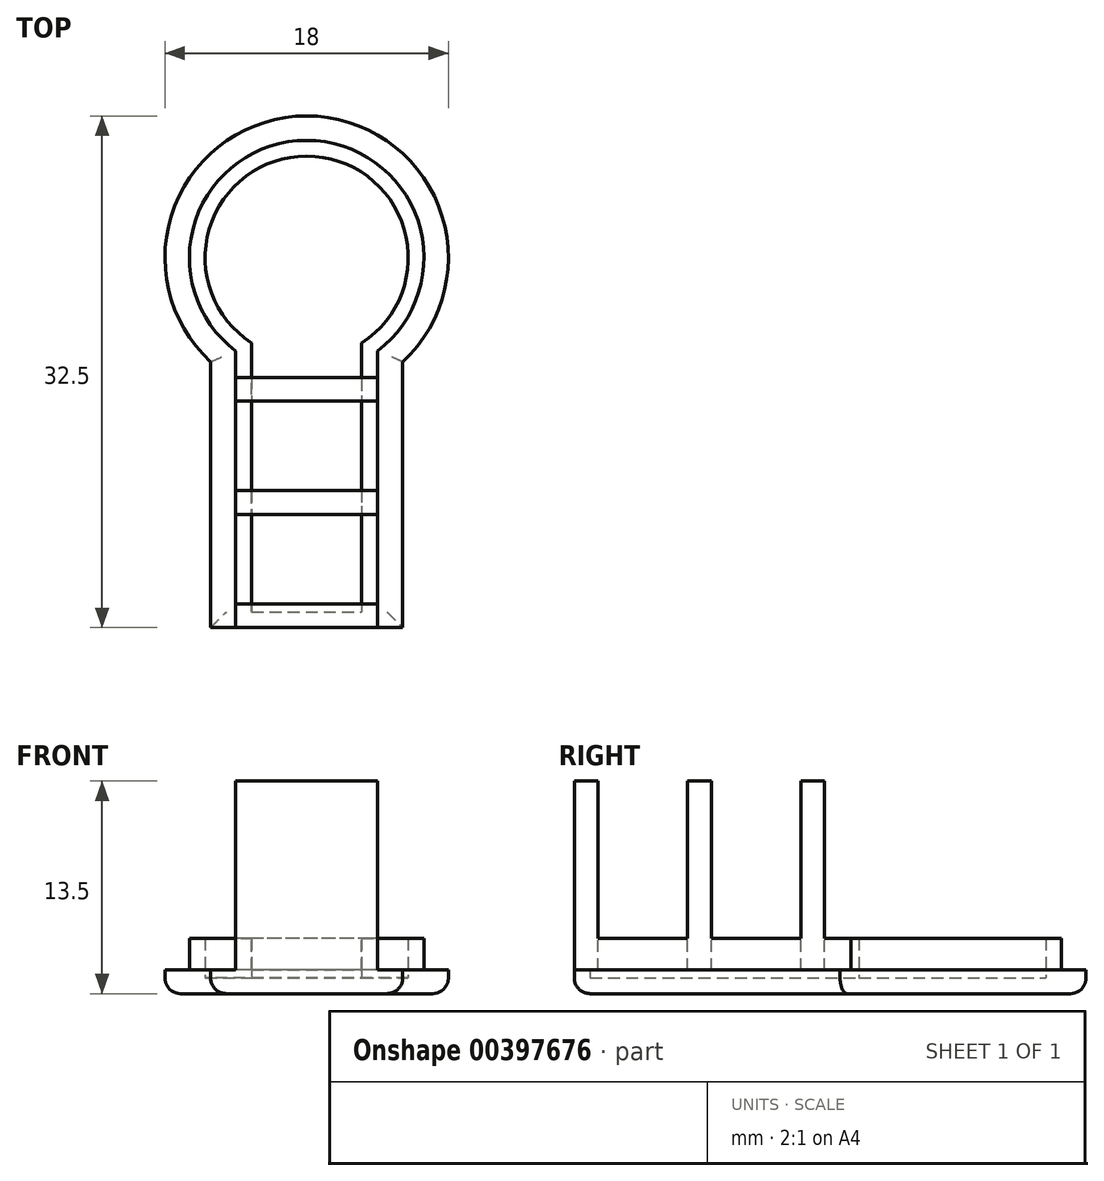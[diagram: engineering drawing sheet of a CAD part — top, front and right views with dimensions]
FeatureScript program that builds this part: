
annotation { "Feature Type Name" : "Feature", "Feature Type Description" : "" }
export const myFeature = defineFeature(function(context is Context, id is Id, definition is map)
    precondition{}
    {
        {
            var Q0;
            Q0=qCreatedBy(makeId("Top.planeOp"),FACE);
            var sketch = newSketch(context, id + "F0", { "sketchPlane" : qUnion([Q0])});
            skArc(sketch, "E0", {"start": v(4.5, -5.94) * mm, "mid": v(0, 7.45) * mm, "end": v(-4.5, -5.94) * mm});
            skLineSegment(sketch, "E1.top", {"start": v(-4.5, -23.5) * mm, "end": v(4.5, -23.5) * mm});
            skLineSegment(sketch, "E1.left", {"start": v(-4.5, -5.94) * mm, "end": v(-4.5, -23.5) * mm});
            skLineSegment(sketch, "E1.right", {"start": v(4.5, -5.94) * mm, "end": v(4.5, -23.5) * mm});
            skSolve(sketch);
        }
        {
            var Q0;
            Q0 = qSketchRegion(id + "F0", true);
            extrude(context, id + "F1", {"entities" : qUnion([Q0]), "depth" : 2 * mm});
        }
        {
            var Q0;
            Q0=qCreatedBy(makeId("Top.planeOp"),FACE);
            var sketch = newSketch(context, id + "F2", { "sketchPlane" : qUnion([Q0])});
            skArc(sketch, "E2", {"start": v(4.5, -5.87) * mm, "mid": v(0, 7.4) * mm, "end": v(-4.5, -5.87) * mm});
            skLineSegment(sketch, "E3.top", {"start": v(-4.5, -23.5) * mm, "end": v(4.5, -23.5) * mm});
            skLineSegment(sketch, "E3.left", {"start": v(-4.5, -5.87) * mm, "end": v(-4.5, -23.5) * mm});
            skLineSegment(sketch, "E3.right", {"start": v(4.5, -5.87) * mm, "end": v(4.5, -23.5) * mm});
            skArc(sketch, "E4.0", {"start": v(6.1, -6.62) * mm, "mid": v(0, 9) * mm, "end": v(-6.1, -6.62) * mm});
            skLineSegment(sketch, "E4.1", {"start": v(6.1, -6.62) * mm, "end": v(6.1, -23.5) * mm});
            skLineSegment(sketch, "E4.3", {"start": v(-6.1, -6.62) * mm, "end": v(-6.1, -23.5) * mm});
            skLineSegment(sketch, "E5", {"start": v(-4.5, -23.5) * mm, "end": v(-6.1, -23.5) * mm});
            skLineSegment(sketch, "E6", {"start": v(-6.1, -23.5) * mm, "end": v(6.1, -23.5) * mm});
            skSolve(sketch);
        }
        {
            var Q0;
            Q0 = qSketchRegion(id + "F2", true);
            extrude(context, id + "F3", {"entities" : qUnion([Q0]), "operationType" : NewBodyOperationType.ADD, "oppositeDirection" : true, "depth" : 1.5 * mm});
        }
        {
            var Q0;
            Q0=makeQuery(id+"F1.opExtrude","CAP_FACE",FACE,{"disambiguationData":[OSD([sQuery(id+"F0.wireOp",EDGE,"E0"),sQuery(id+"F0.wireOp",EDGE,"E1.top"),sQuery(id+"F0.wireOp",EDGE,"E1.left"),sQuery(id+"F0.wireOp",EDGE,"E1.right")])],"isStart":false});
            shell(context, id + "F4", {"entities" : qUnion([Q0]), "thickness" : 1 * mm});
        }
        {
            var Q0;
            Q0=qCreatedBy(makeId("Top.planeOp"),FACE);
            var sketch = newSketch(context, id + "F5", { "sketchPlane" : qUnion([Q0])});
            skLineSegment(sketch, "E7.bottom", {"start": v(-4.5, -7.6) * mm, "end": v(4.5, -7.6) * mm});
            skLineSegment(sketch, "E7.top", {"start": v(-4.5, -9.1) * mm, "end": v(4.5, -9.1) * mm});
            skLineSegment(sketch, "E7.left", {"start": v(-4.5, -7.6) * mm, "end": v(-4.5, -9.1) * mm});
            skLineSegment(sketch, "E7.right", {"start": v(4.5, -7.6) * mm, "end": v(4.5, -9.1) * mm});
            skLineSegment(sketch, "E8.0.1.0", {"start": v(-4.5, -14.8) * mm, "end": v(4.5, -14.8) * mm});
            skLineSegment(sketch, "E8.0.1.1", {"start": v(-4.5, -14.8) * mm, "end": v(-4.5, -16.3) * mm});
            skLineSegment(sketch, "E8.0.1.2", {"start": v(-4.5, -16.3) * mm, "end": v(4.5, -16.3) * mm});
            skLineSegment(sketch, "E8.0.1.3", {"start": v(4.5, -14.8) * mm, "end": v(4.5, -16.3) * mm});
            skLineSegment(sketch, "E8.0.2.0", {"start": v(-4.5, -22) * mm, "end": v(4.5, -22) * mm});
            skLineSegment(sketch, "E8.0.2.1", {"start": v(-4.5, -22) * mm, "end": v(-4.5, -23.5) * mm});
            skLineSegment(sketch, "E8.0.2.2", {"start": v(-4.5, -23.5) * mm, "end": v(4.5, -23.5) * mm});
            skLineSegment(sketch, "E8.0.2.3", {"start": v(4.5, -22) * mm, "end": v(4.5, -23.5) * mm});
            skLineSegment(sketch, "E8.direction1", {"start": v(-4.5, -7.6) * mm, "end": v(2.84, -7.6) * mm, "construction": true});
            skLineSegment(sketch, "E8.direction2", {"start": v(-4.5, -7.6) * mm, "end": v(-4.5, -14.8) * mm, "construction": true});
            skSolve(sketch);
        }
        {
            var Q0;
            Q0 = qSketchRegion(id + "F5", true);
            extrude(context, id + "F6", {"entities" : qUnion([Q0]), "operationType" : NewBodyOperationType.ADD, "depth" : 12 * mm});
        }
        {
            var Q0;
            Q0=makeQuery(id+"F3.opExtrude","CAP_EDGE",EDGE,{"disambiguationData":[OSD([sQuery(id+"F2.wireOp",EDGE,"E4.0")])],"isStart":false});
            var Q1;
            Q1=makeQuery(id+"F3.opExtrude","CAP_EDGE",EDGE,{"disambiguationData":[OSD([sQuery(id+"F2.wireOp",EDGE,"E4.1")])],"isStart":false});
            var Q2;
            Q2=makeQuery(id+"F3.opExtrude","CAP_EDGE",EDGE,{"disambiguationData":[OSD([sQuery(id+"F2.wireOp",EDGE,"E6")])],"isStart":false});
            var Q3;
            Q3=makeQuery(id+"F3.opExtrude","CAP_EDGE",EDGE,{"disambiguationData":[OSD([sQuery(id+"F2.wireOp",EDGE,"E4.3")])],"isStart":false});
            fillet(context, id + "F7", {"entities" : qUnion([Q0, Q1, Q2, Q3]), "radius" : 1 * mm, "tangentPropagation" : true, "allowEdgeOverflow" : false});
        }
    });
